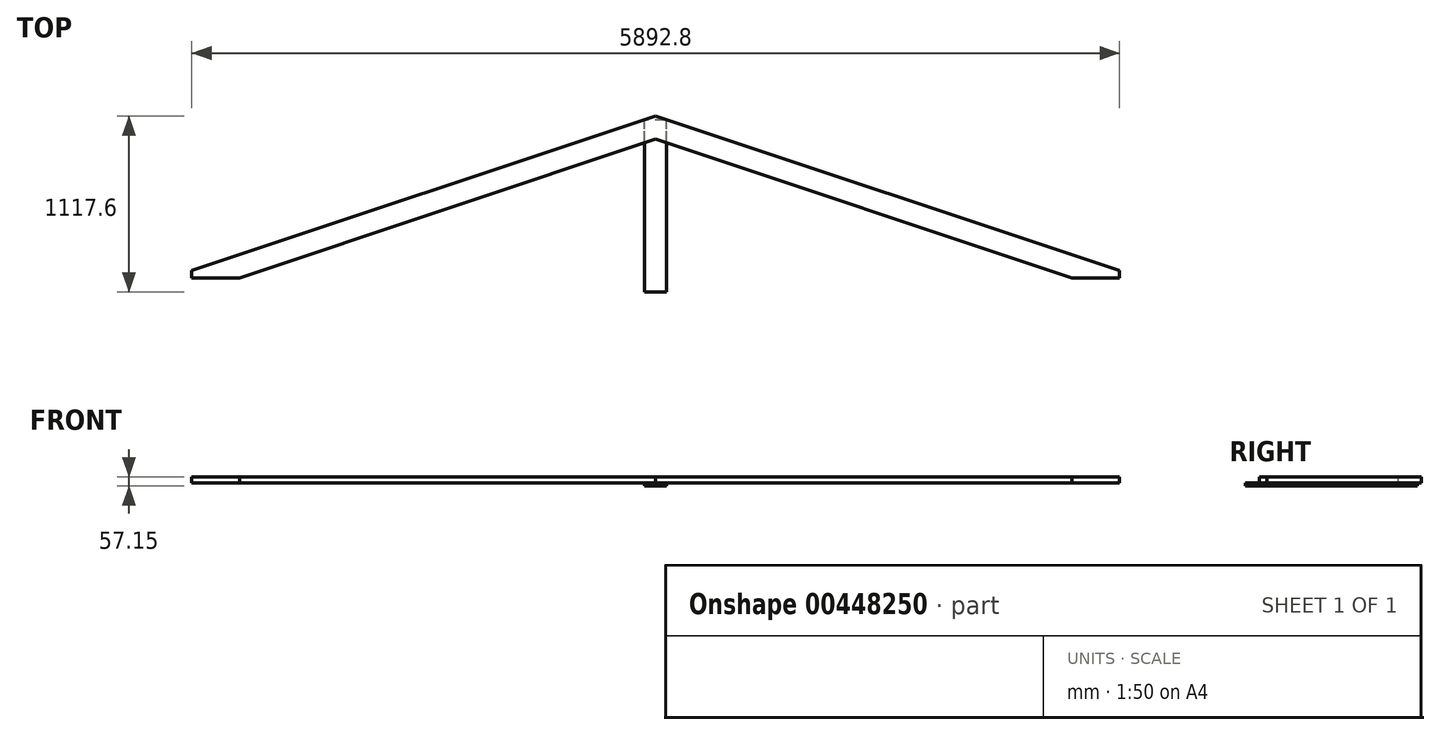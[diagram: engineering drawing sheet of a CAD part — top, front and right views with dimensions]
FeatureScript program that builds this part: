
annotation { "Feature Type Name" : "Feature", "Feature Type Description" : "" }
export const myFeature = defineFeature(function(context is Context, id is Id, definition is map)
    precondition{}
    {
        {
            var Q0;
            Q0=qCreatedBy(makeId("Top.planeOp"),FACE);
            var sketch = newSketch(context, id + "F0", { "sketchPlane" : qUnion([Q0])});
            skLineSegment(sketch, "E0.bottom", {"start": v(-2946.4, 0) * mm, "end": v(2946.4, 0) * mm});
            skLineSegment(sketch, "E0.top", {"start": v(-2946.4, 88.9) * mm, "end": v(2946.4, 88.9) * mm});
            skLineSegment(sketch, "E0.left", {"start": v(-2946.4, 0) * mm, "end": v(-2946.4, 88.9) * mm});
            skLineSegment(sketch, "E0.right", {"start": v(2946.4, 0) * mm, "end": v(2946.4, 88.9) * mm});
            skSolve(sketch);
        }
        {
            var Q0;
            Q0=makeQuery(id+"F0.imprint","IMPRINT",FACE,{"disambiguationData":[TD([[makeQuery(id+"F0.imprint","IMPRINT",EDGE,{"derivedFrom":sQuery(id+"F0.wireOp",EDGE,"E0.bottom")}),1.0]])]});
            extrude(context, id + "F1", {"entities" : qUnion([Q0]), "depth" : 38.1 * mm});
        }
        {
            var Q0;
            Q0=qCreatedBy(makeId("Top.planeOp"),FACE);
            var sketch = newSketch(context, id + "F2", { "sketchPlane" : qUnion([Q0])});
            skLineSegment(sketch, "E1.bottom", {"start": v(69.85, 0) * mm, "end": v(-69.85, 0) * mm});
            skLineSegment(sketch, "E1.top", {"start": v(69.85, 1092.2) * mm, "end": v(-69.85, 1092.2) * mm});
            skLineSegment(sketch, "E1.left", {"start": v(69.85, 0) * mm, "end": v(69.85, 1092.2) * mm});
            skLineSegment(sketch, "E1.right", {"start": v(-69.85, 0) * mm, "end": v(-69.85, 1092.2) * mm});
            skSolve(sketch);
        }
        {
            var Q0;
            Q0 = qSketchRegion(id + "F2", true);
            extrude(context, id + "F3", {"entities" : qUnion([Q0]), "oppositeDirection" : true, "depth" : 19.05 * mm});
        }
        {
            var Q0;
            Q0=makeQuery(id+"F1.opExtrude","CAP_FACE",FACE,{"disambiguationData":[OSD([sQuery(id+"F0.wireOp",EDGE,"E0.bottom"),sQuery(id+"F0.wireOp",EDGE,"E0.top"),sQuery(id+"F0.wireOp",EDGE,"E0.left"),sQuery(id+"F0.wireOp",EDGE,"E0.right")])],"isStart":false});
            var sketch = newSketch(context, id + "F4", { "sketchPlane" : qUnion([Q0])});
            skLineSegment(sketch, "E2", {"start": v(-2946.4, 0) * mm, "end": v(-2946.4, 135.46) * mm});
            skLineSegment(sketch, "E3", {"start": v(-2946.4, 135.46) * mm, "end": v(0, 1117.6) * mm});
            skLineSegment(sketch, "E4", {"start": v(0, 1117.6) * mm, "end": v(0, 970.34) * mm});
            skLineSegment(sketch, "E5", {"start": v(0, 970.34) * mm, "end": v(-2911.02, 0) * mm});
            skLineSegment(sketch, "E6", {"start": v(-2911.02, 0) * mm, "end": v(-2946.4, 0) * mm});
            skLineSegment(sketch, "E7.MirrorCS", {"start": v(2911.02, 0) * mm, "end": v(2946.4, 0) * mm});
            skLineSegment(sketch, "E8.MirrorCS", {"start": v(2946.4, 0) * mm, "end": v(2946.4, 135.46) * mm});
            skLineSegment(sketch, "E9.MirrorCS", {"start": v(2946.4, 135.46) * mm, "end": v(0, 1117.6) * mm});
            skLineSegment(sketch, "E10.MirrorCS", {"start": v(0, 970.34) * mm, "end": v(2911.02, 0) * mm});
            skSolve(sketch);
        }
        {
            var Q0;
            Q0 = qSketchRegion(id + "F4", true);
            extrude(context, id + "F5", {"entities" : qUnion([Q0]), "oppositeDirection" : true, "depth" : 38.1 * mm});
        }
        {
            var Q0;
            Q0=makeQuery(id+"F5.opExtrude","CAP_FACE",FACE,{"disambiguationData":[OSD([sQuery(id+"F4.wireOp",EDGE,"E2"),sQuery(id+"F4.wireOp",EDGE,"E3"),sQuery(id+"F4.wireOp",EDGE,"E5"),sQuery(id+"F4.wireOp",EDGE,"E6"),sQuery(id+"F4.wireOp",EDGE,"E7.MirrorCS"),sQuery(id+"F4.wireOp",EDGE,"E8.MirrorCS"),sQuery(id+"F4.wireOp",EDGE,"E9.MirrorCS"),sQuery(id+"F4.wireOp",EDGE,"E10.MirrorCS")])],"isStart":false});
            var sketch = newSketch(context, id + "F6", { "sketchPlane" : qUnion([Q0])});
            skLineSegment(sketch, "E11", {"start": v(2946.4, -88.9) * mm, "end": v(-2946.4, -88.9) * mm});
            skLineSegment(sketch, "E12", {"start": v(2946.4, -88.9) * mm, "end": v(2946.4, 0) * mm});
            skLineSegment(sketch, "E13", {"start": v(2946.4, 0) * mm, "end": v(-2946.4, 0) * mm});
            skLineSegment(sketch, "E14", {"start": v(-2946.4, 0) * mm, "end": v(-2946.4, -88.9) * mm});
            skSolve(sketch);
        }
        {
            var Q0;
            Q0 = qSketchRegion(id + "F6", true);
            extrude(context, id + "F7", {"entities" : qUnion([Q0]), "operationType" : NewBodyOperationType.REMOVE, "endBound" : BoundingType.THROUGH_ALL, "oppositeDirection" : true, "depth" : 25.4 * mm});
        }
    });
